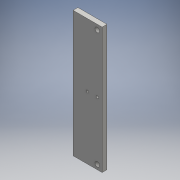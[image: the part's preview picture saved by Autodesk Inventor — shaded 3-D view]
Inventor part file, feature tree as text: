
AUTODESK INVENTOR PART (.ipt)
format: ipt  version: 2016 (Build 200138000, 138)  size: 111,104 bytes
history: native  units: mm
features: extrude x2, sketch x1
ambient origin geometry x8: Origin, YZ Plane, XZ Plane, XY Plane, X Axis, Y Axis, Z Axis, Center Point
bodies: Body1 (feature_tree)
feature tree (3):
  sketch  "スケッチ1"
  extrude  "押し出し2"  Depth=12.0mm
  extrude  "押し出し3"  Depth=52.0mm
